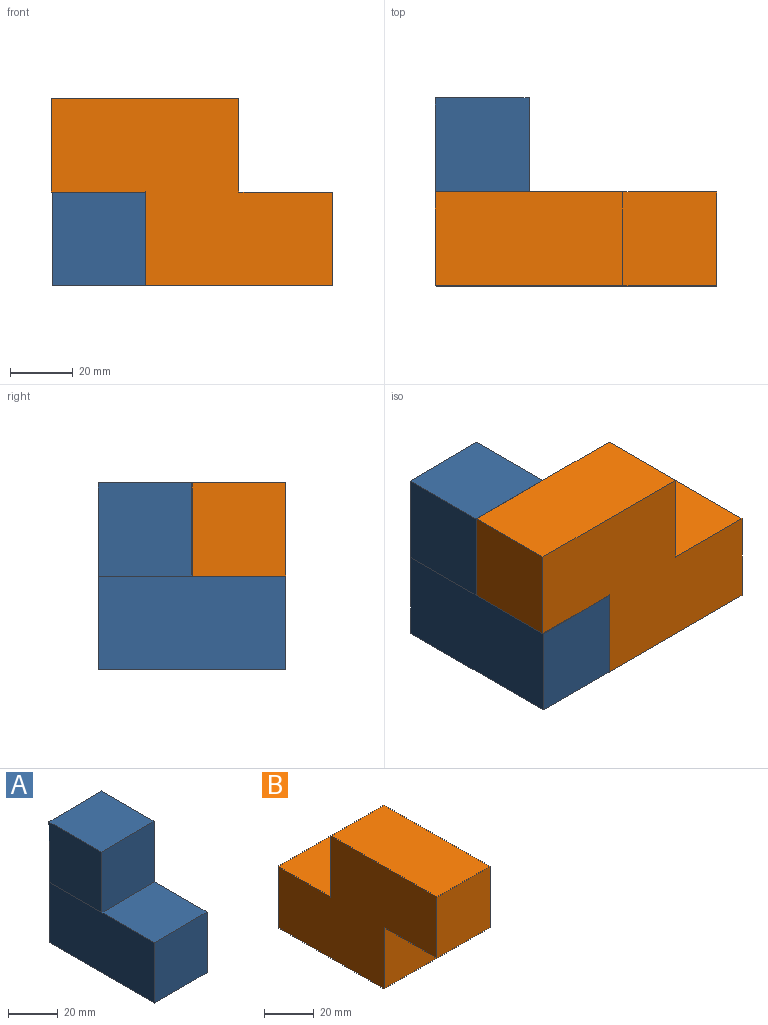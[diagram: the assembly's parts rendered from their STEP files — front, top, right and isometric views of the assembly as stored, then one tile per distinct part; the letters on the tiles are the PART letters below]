
ASSEMBLY  parts=2 mates=1
PART A: 10 faces, bbox 30.3x60x60 mm
  f0: plane 30x30mm, normal (-0.01,0,1), area 900mm2, adj f1,f3,f4,f7
  f1: plane 60x29.72mm, normal (-1,0,0), area 1783.4mm2, adj f0,f2,f4,f5,f6
  f2: plane 60x30mm, normal (0,0,-1), area 1799.9mm2, adj f1,f3,f4,f5
  f3: plane 60x30mm, normal (1,0,0), area 1800mm2, adj f0,f2,f4,f5,f8
  f4: plane 30x30mm, normal (0,-1,0), area 895.8mm2, adj f0,f1,f2,f3
  f5: plane 60x30.28mm, normal (0,1,0), area 1795.8mm2, adj f1,f2,f3,f6,f8,f9
  f6: plane 30x30mm, normal (-1,0,-0.01), area 900mm2, adj f1,f5,f7,f9
  f7: plane 30.28x30.28mm, normal (0,-1,0), area 900mm2, adj f0,f6,f8,f9
  f8: plane 30x30mm, normal (1,0,0.01), area 900mm2, adj f3,f5,f7,f9
  f9: plane 30x30mm, normal (-0.01,0,1), area 900mm2, adj f5,f6,f7,f8
PART B: 10 faces, bbox 30x90x60 mm
  f0: plane 30x30mm, normal (0,1,0), area 900mm2, adj f2,f3,f4,f8
  f1: plane 30x30mm, normal (0,0,-1), area 900mm2, adj f3,f4,f5,f6
  f2: plane 60x30mm, normal (0,0,1), area 1800mm2, adj f0,f3,f4,f5
  f3: plane 90x60mm, normal (-1,0,0), area 3600mm2, adj f0,f1,f2,f5,f6,f7,f8,f9
  f4: plane 90x60mm, normal (1,0,0), area 3600mm2, adj f0,f1,f2,f5,f6,f7,f8,f9
  f5: plane 30x30mm, normal (0,-1,0), area 900mm2, adj f1,f2,f3,f4
  f6: plane 30x30mm, normal (0,-1,0), area 900mm2, adj f1,f3,f4,f7
  f7: plane 60x30mm, normal (0,0,-1), area 1800mm2, adj f3,f4,f6,f9
  f8: plane 30x30mm, normal (0,0,1), area 900mm2, adj f0,f3,f4,f9
  f9: plane 30x30mm, normal (0,1,0), area 900mm2, adj f3,f4,f7,f8
PLACE A t=(-0.02,0.96,-2.6)mm
PLACE B rot(axis=(0,0,-1),90deg) t=(13.13,-61.19,25.33)mm
MATE fastened A.f7 <-> B.f3  axis (0,-1,0) through (-16.87,-29.04,55.33)mm
